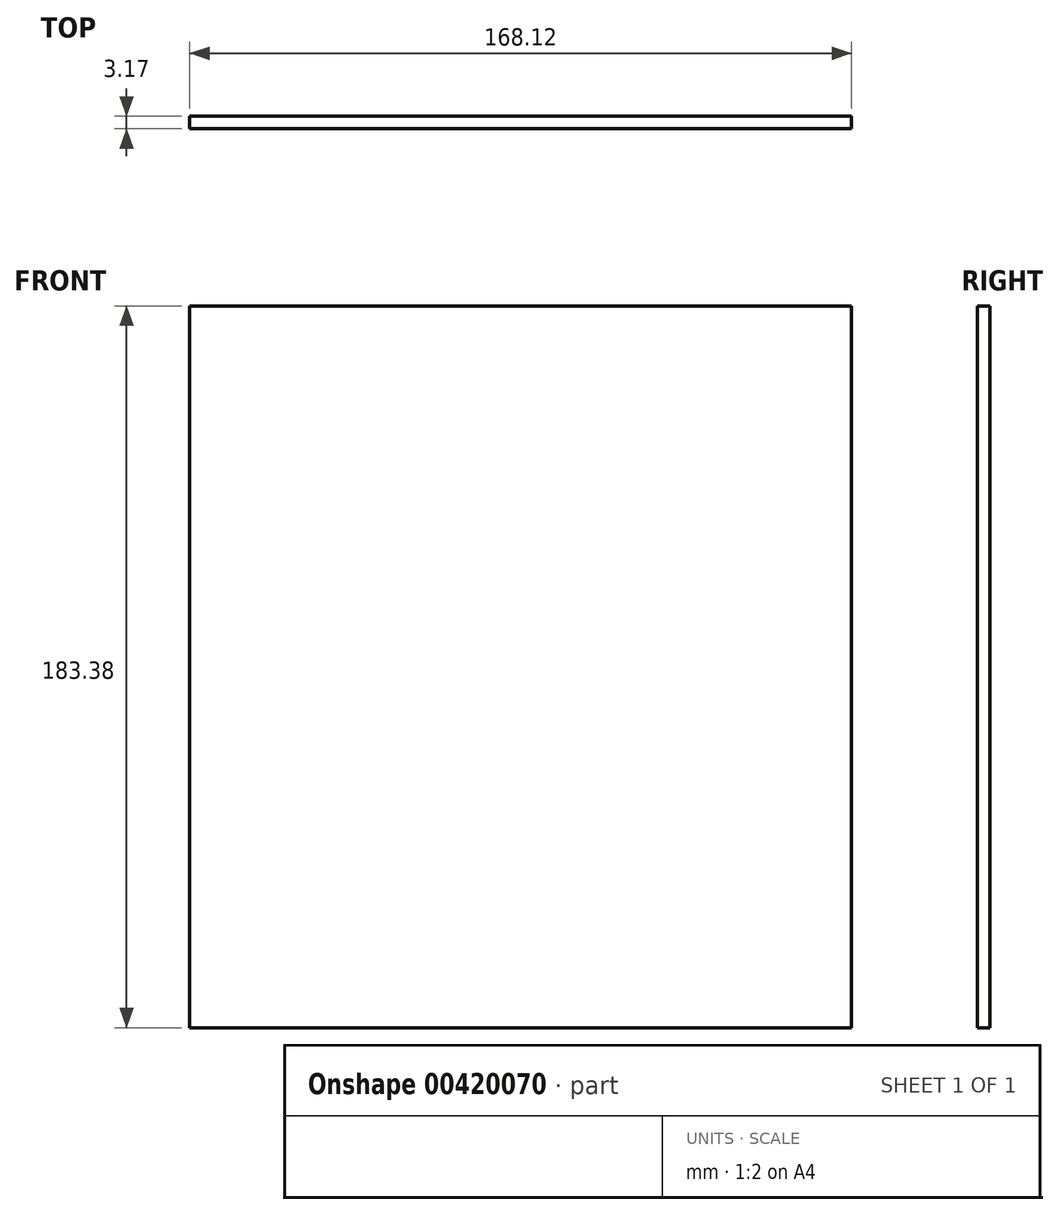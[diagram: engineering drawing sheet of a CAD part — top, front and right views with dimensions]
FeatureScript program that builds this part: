
annotation { "Feature Type Name" : "Feature", "Feature Type Description" : "" }
export const myFeature = defineFeature(function(context is Context, id is Id, definition is map)
    precondition{}
    {
        {
            var Q0;
            Q0=qCreatedBy(makeId("Front.planeOp"),FACE);
            var sketch = newSketch(context, id + "F0", { "sketchPlane" : qUnion([Q0])});
            skLineSegment(sketch, "E0.bottom", {"start": v(84.06, 91.69) * mm, "end": v(-84.06, 91.69) * mm});
            skLineSegment(sketch, "E0.top", {"start": v(84.06, -91.69) * mm, "end": v(-84.06, -91.69) * mm});
            skLineSegment(sketch, "E0.left", {"start": v(84.06, 91.69) * mm, "end": v(84.06, -91.69) * mm});
            skLineSegment(sketch, "E0.right", {"start": v(-84.06, 91.69) * mm, "end": v(-84.06, -91.69) * mm});
            skPoint(sketch, "E0.middle", {"position": v(0, 0) * mm});
            skSolve(sketch);
        }
        {
            var Q0;
            Q0 = qSketchRegion(id + "F0", true);
            extrude(context, id + "F1", {"entities" : qUnion([Q0]), "depth" : 3.17 * mm});
        }
    });
